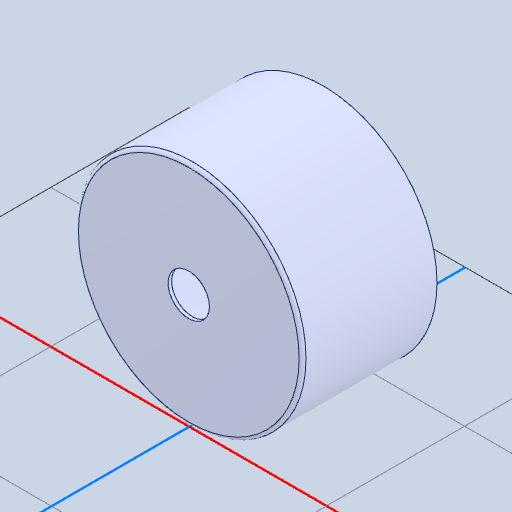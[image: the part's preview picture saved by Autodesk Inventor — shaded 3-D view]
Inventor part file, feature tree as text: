
AUTODESK INVENTOR PART (.ipt)
format: ipt  version: 2022 (Build 260153000, 153)  size: 121,856 bytes
history: native  units: mm
features: other x1, fillet x1
ambient origin geometry x8: Origin, YZ Plane, XZ Plane, XY Plane, X Axis, Y Axis, Z Axis, Center Point
bodies: Body1 (feature_tree)
feature tree (2):
  other  "Твердое тело1"
  fillet  "Fillet1"  [1 undecoded]
note: 1 required parameter value undecoded (feature->parameter linkage not recoverable at this tier; creation-order binding heuristic only, values carry confidence <= 0.55)
